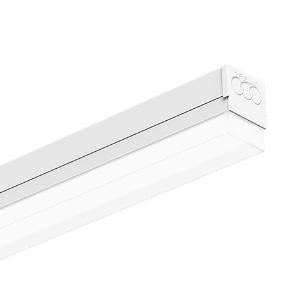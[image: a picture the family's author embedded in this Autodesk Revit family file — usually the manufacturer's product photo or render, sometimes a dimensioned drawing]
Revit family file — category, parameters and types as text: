
# Revit family: 3f_filippi_-_3f_linux_dr_3f_filippi_-_a20511_-_3f_linux_dr_2x30_led_l1778
name_source: partatom
category: Lighting Fixtures
units: mm (PartAtom-declared; Revit-internal decimal feet)

## family parameters
Cut with Voids When Loaded = No
Host = Face
Light Source = No
Part Type = Normal
Room Calculation Point = No
Round Connector Dimension = Use Diameter
Shared = No

## types (1)
- 3F Filippi - 3F Linux DR (1 x LED, 7856 lm, 66 W, 4000 K)
    Apparent Load = 66 VA
    Approval mark = CE
    CIE Flux Codes = 41 72 91 86 100
    Color Rendering = 80
    Color Temperature = 4000 K
    Control Gear = Electronic ballast
    Default Elevation = 1800 mm
    Description = Light unit for structure continues 3F Linux S.

ILLUMINOTECHNICAL
Luminous efficiency 100% (DLOR 86%, ULOR 14%).
Initial luminous flux of the luminaire 7856 lm.
Diffused symmetric distribution.
Installation Interdistance Transv.D = 1.38 x hu - Long.D = 1.25 x hu.
Tabular UGR (CIE 117 - 4H-8H; S=0.25H; 70/50/20): RUG 25.8 - 24.4.
Beam angle: 136° - 112°.
Luminous efficacy 119 lm/W.
Lifetime (L93/B10): 30000 h. (tq+25°C)
Lifetime (L90/B10): 50000 h. (tq+25°C)
Lifetime (L85/B10): 80000 h. (tq+25°C)
Lifetime (L80/B10): 100000 h. (tq+25°C)
Sudden decreased luminous flux after 50000 hours: 0% (C0).
Photobiological safety in compliance with IEC/TR 62778: RG0 risk exempt, (IEC 62471).
In compliance with IEC/EN 62722-2-1 - IEC/EN 62717 standards.

SOURCE
2 linear LED modules 30W/840.
Energy efficiency class (UE 2019/2020 - UE 2019/2015): D.
CIE 13.3 Colour rendering index: CRI >80 (R9 <50%).
IES TM-30 Fidelity Index: Rf = 84 Rg = 95.
CCT nominal colour temperature 4000 K.
Colour initial tolerance (MacAdam): SDCM 3.

MECHANICAL
Light unit in hot-galvanised steel, painted in white polyester base with fixing springs and retractable safety hooks in stainless steel.
Rectangular screen in self-extinguishing polycarbonate, UV stabilised, opal, with smooth outer surface.
Luminaire with limited surface temperature. - D - (EN 60598-2-24)
Dimensions: 1778x62 mm, height 81 mm. Weight 2.515 kg.
IP40 protection degree.
Mechanical strength to impacts IK06 (1 joule).
Glow-wire test resistance 850°C.

ELECTRICAL
Halogen Free electronic wiring 230V-50/60Hz, power factor 0.95, THD <25%, constant output current, SELV, class I, 1 driver.
Power of the luminaire 66 W.
ENEC - CE.
SAFE FLICKER: PstLM=<1 and SVM=<0.4 (IEC TR 61547-1 and IEC TR 63158), to ensure a more comfortable and safe light.
Luminaire compliant with EN 60598-2-22 for power supply from a centralised emergency system CPSS (Central Power Supply System), not incorporated in the luminaire - high risk areas excluded. The default power and flux are 100% in AC and 100% in DC.
Ambient temperature from 0°C to +30°C.
Temperature class T6 max 85°C.
Connection to the structure with 3-pin plug with phase selection (H05Z-U Halogen Free cable section 0.5 mm² HT90).
Relative humidity UR: <85%.

INSTALLATION
Ceiling / Suspended / Wall.
All accessories dedicated to this product are available on the Catalog and on our website www.3F-Filippi.com.

STRUCTURE
Hot-galvanised wired structure, painted in polyester base white, obtained through rolling process.
Saline-mist resistance equal to 300hrs and damp resistance equal to 700hrs.
Through-wiring 5 or 7 poles with cables H07Z-U Halogen Free section 2.5 mm² HT90, with quick connecting terminal, irreversible, start / end and intermediate power towers.
Linear connecting element in hot galvanised steel already mounted on one end to form continuous channels, only L3556 structures.
A20017 - 3F Linux S 5P L3556, structure with through-wiring 5-pole.
A20019 - 3F Linux S 5P L1778, structure with through-wiring 5-pole.
A20024 - 3F Linux S 7P L3556, structure with through-wiring 7-pole.
A20026 - 3F Linux S 7P L1778, structure with through-wiring 7-pole.

APPLICATIONS
Suitable product for food production plants (HACCP), IFS (Food Version 6), BRC (GSFS Food Version 7).
In commercial environments, exhibition areas, shops and stores.

WARNING
Luminaire designed for disposal/recycling at end-of-life.
Replaceable (LED only) light source by a professional. Replaceable control gear by a professional.
    Height = 81 mm
    Lamp = 1 x LED
    Lamp Light Flux = 7856 lm
    Lamp Power = 66 W
    Lamp count = 1
    Length = 1778 mm
    Lifetime = 50000 h
    Luminous efficacy = 119 lm/W
    Manufacturer = 3F Filippi
    ModVariant = No
    Model = 3F Filippi - A20511 - 3F Linux DR 2x30 LED L1778
    Mounting Place = Ceiling
    Mounting Type = Pendant
    Number of Poles = 1
    OnlyDefault = Yes
    Power Factor = 1
    Product Name = 3F Filippi - 3F Linux DR
    Product group = pendant luminaire
    ProductGroupID = 9
    Protection Class = Protection class I
    Protection Degree = IP 40
    RLX_Detail_Level = 1
    RLX_Emergency_Light_Flux = 0 lm
    RLX_Emergency_Type = 0
    RLX_Emergency_Type_DB = No
    RlxData = <blob elided: 33909 chars, md5=3117e6f6>
    Socket = socket
    Standby Power = 0 W
    System Light Flux = 7856 lm
    System Power = 66 W
    Type Comments = Product without accessories
    Type Image = 3ffilippi_3f_linux_dr.jpg
    URL = http://relux.com
    VarID = ---
    Voltage = 0 V
    Weight = 0.00 kg
    Width = 62 mm  [stored 0.203412 ft]

note: [stored X ft] marks values corroborated as IEEE doubles in the binary element streams (Revit-internal decimal feet)

## geometry (parser evidence)
native form markers: Blend x4, Sweep x11
no freeform markers — native parametric forms only
